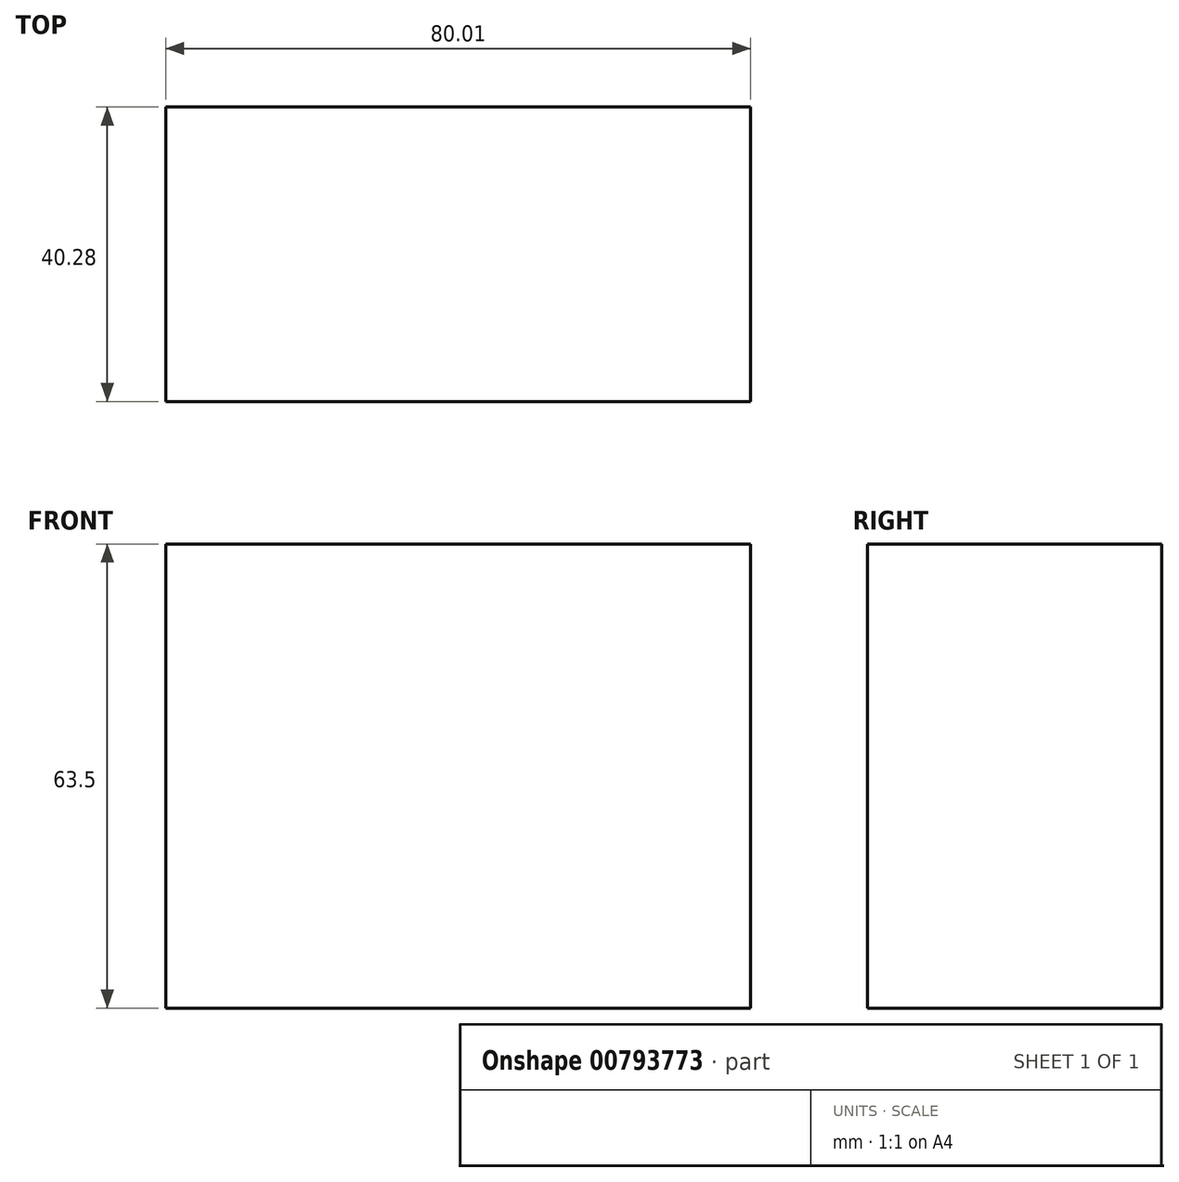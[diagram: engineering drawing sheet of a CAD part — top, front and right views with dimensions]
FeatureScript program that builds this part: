
annotation { "Feature Type Name" : "Feature", "Feature Type Description" : "" }
export const myFeature = defineFeature(function(context is Context, id is Id, definition is map)
    precondition{}
    {
        {
            var Q0;
            Q0=qCreatedBy(makeId("Top.planeOp"),FACE);
            var sketch = newSketch(context, id + "F0", { "sketchPlane" : qUnion([Q0])});
            skLineSegment(sketch, "E0.bottom", {"start": v(-53.3, 34.55) * mm, "end": v(26.72, 34.55) * mm});
            skLineSegment(sketch, "E0.top", {"start": v(-53.3, -5.73) * mm, "end": v(26.72, -5.73) * mm});
            skLineSegment(sketch, "E0.left", {"start": v(-53.3, 34.55) * mm, "end": v(-53.3, -5.73) * mm});
            skLineSegment(sketch, "E0.right", {"start": v(26.72, 34.55) * mm, "end": v(26.72, -5.73) * mm});
            skSolve(sketch);
        }
        {
            var Q0;
            Q0=makeQuery(id+"F0.imprint","IMPRINT",FACE,{"disambiguationData":[TD([[makeQuery(id+"F0.imprint","IMPRINT",EDGE,{"derivedFrom":sQuery(id+"F0.wireOp",EDGE,"E0.bottom")}),-1.0]])]});
            extrude(context, id + "F1", {"entities" : qUnion([Q0]), "depth" : 63.5 * mm, "offsetDistance" : 25.4 * mm});
        }
    });
